# Revit family: 05-2759-05-05
name_source: partatom
category: Luminarias
revit_build: Autodesk Revit 2017 (Build: 20160225_1515(x64)
units: mm (PartAtom-declared; Revit-internal decimal feet)

## family parameters
Anfitrión = Cara
Compartido = Sí
Corte con vacíos al cargar = No
Cota de conector redondo = Diámetro de uso
Número OmniClass = 23.80.70.00
Origen de luz = No
Punto de cálculo de habitación = No
Tipo de pieza = Normal
Título OmniClass = Lighting

## types (1)
- 05-2759-05-05
    Acabado = Negro
    CRI = 0
    Carga aparente = 0 VA
    Catálogo = Decorative
    CodigoGubimclass = 50.60.50.20
    CodigoOmniclass = 21-04 50 40
    CodigoUniclass2015 = EF_70_80
    CodigoUniformat2010 = D5040
    DescripcionGubimclass = Iluminación interior
    DescripcionOmniclass = Lighting
    DescripcionUniclass2015 = Lighting
    DescripcionUniformat2010 = Lighting
    EAN13 = 8435526847389
    Eficiencia energética = NO BULB
    Elevación por defecto = 1000 mm  [stored 3.28084 ft]
    Etiqueta V/f = 220-240V/50-60Hz
    Fabricante = LEDS C4
    Familia = Pipe Wall Fixture
    FechaVersion = Julio 2020
    Ficha = http://files.leds-c4.com
    Fotometría = http://files.leds-c4.com
    IMC = http://files.leds-c4.com
    IP = IP23
    IfcExportAs = IfcLightFixture
IfcLightFixture
    IfcExportType = NOTDEFINED
    Imagen web = http://files.leds-c4.com
    LDT = http://files.leds-c4.com
    Lumenes reales (lm) = 0
    Material = Aluminio, Acero
    Peso neto (KG) = 0.55
    Pluma comercial = http://files.leds-c4.com
    Producto descatalogado = Catalogado ES
    Referencia = 05-2759-05-05
    Tender text (Castellano) = LEDS C4
Pipe Wall Fixture
05-2759-05-05

Aplique de uso interior para iluminar hacia arriba y hacia abajo 

Ideal composiciones deco-tech. Diseño minimalista. Muy versátil. Múltiples instalaciones. Muy customizable: accesorios, acabados… Òptimo precio-rendimiento. Òptimo confort visual. Doble instalación empotrado/superficie. Fácil instalación. Colección completa con productos complementarios. Alta durabilidad para uso intensivo. Material estructura: Aluminio, Acero. Acabado estructura: Negro. Garantía: 5 Años.

Peso neto del producto (Kg): 0.550
Anchura o diámetro del producto (mm): 68
Altura del producto (mm): 200
Salida del producto (mm): 85

Clase 1. Prueba hilo incandescente: 850. IP: IP23. GU10. Nº de portalámparas o Leds: 2. Potencia máxima de la fuente de luz: 50W. Potencia total: 1000.
    Tender text (English) = LEDS C4
Pipe Wall Fixture
05-2759-05-05

Wall light for indoor use. 

For uplighting and downlighting. Ideal deco-tech compositions. Minimalist design. Highly versatile, multiple installations. Highly customisable: accessories, finishes… Optimum price-performance. Optimum visual comfort. Embedded/surface mounted double installation. Easy instalation. Full collection with complementary products. High durability for intensive use. Structure material: Aluminium, Steel. Structure finish: Black. Warranty: 5 Years.

Product net weight (Kg): 0.550
Product width or diameter (mm): 68
Product height (mm): 200
Product aperture (mm): 85

Class 1. Glow wire test: 850. IP: IP23. GU10. No. of lampholders or LEDs: 2. Maximum power of light source: 50W. Total power: 1000.
    Tipo = Aplique
    Vatios (W) = 1000
    Versión = v1

note: [stored X ft] marks values corroborated as IEEE doubles in the binary element streams (Revit-internal decimal feet)
